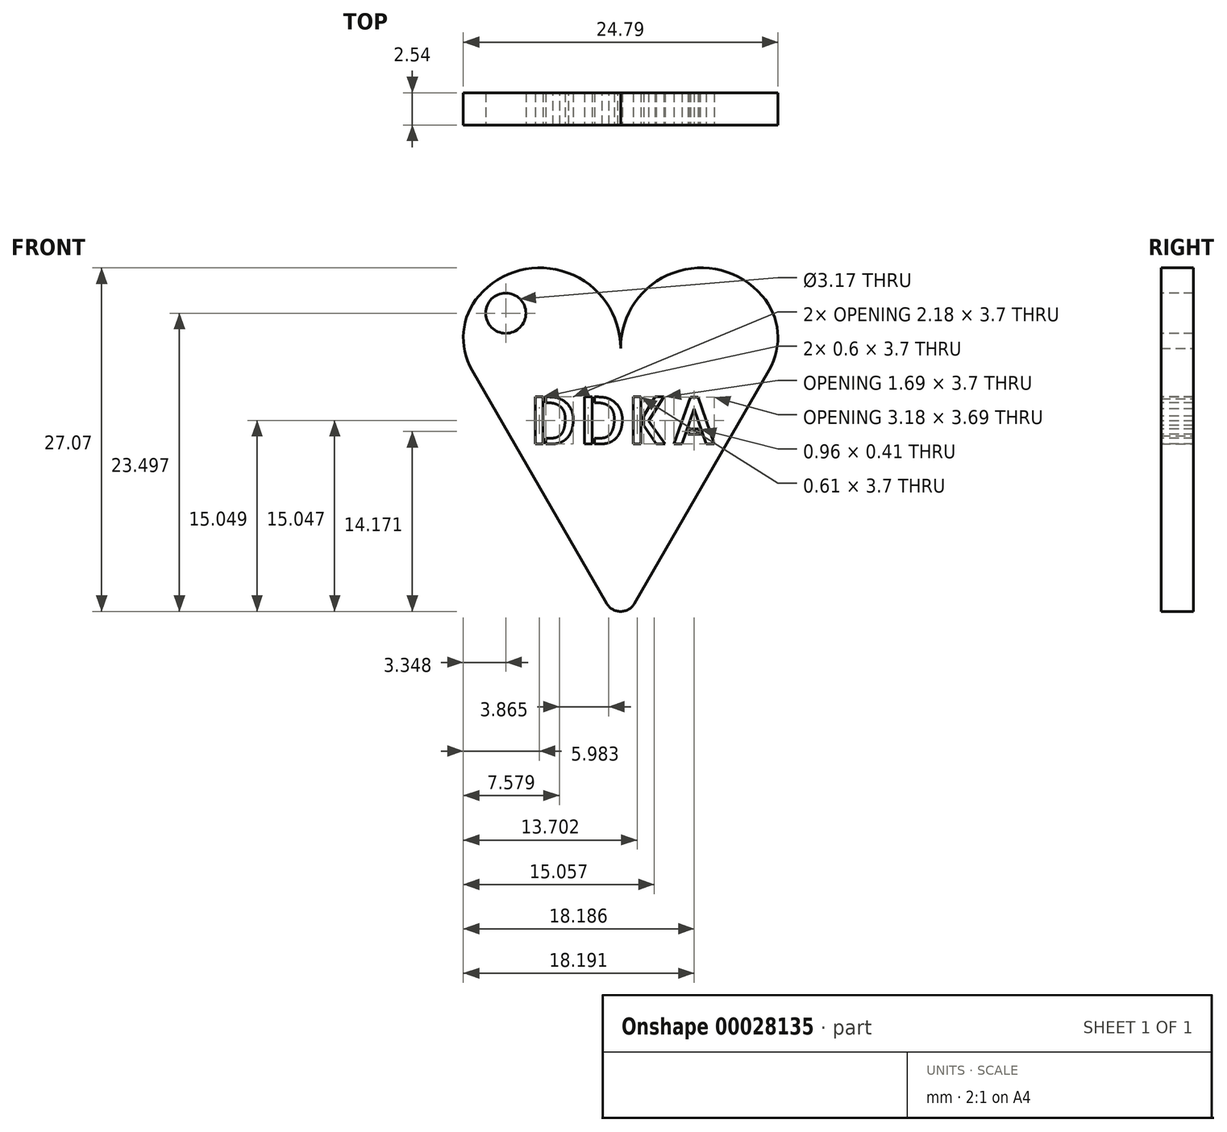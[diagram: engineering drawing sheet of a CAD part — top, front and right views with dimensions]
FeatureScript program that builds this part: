
annotation { "Feature Type Name" : "Feature", "Feature Type Description" : "" }
export const myFeature = defineFeature(function(context is Context, id is Id, definition is map)
    precondition{}
    {
        {
            var Q0;
            Q0=qCreatedBy(makeId("Front.planeOp"),FACE);
            var sketch = newSketch(context, id + "F0", { "sketchPlane" : qUnion([Q0])});
            skLineSegment(sketch, "E0", {"start": v(-11.28, 6.27) * mm, "end": v(1.42, -15.72) * mm});
            skLineSegment(sketch, "E1", {"start": v(1.42, -15.72) * mm, "end": v(14.12, 6.27) * mm});
            skLineSegment(sketch, "E2", {"start": v(14.12, 6.27) * mm, "end": v(-11.28, 6.27) * mm});
            skLineSegment(sketch, "E3", {"start": v(1.42, -15.72) * mm, "end": v(1.42, 38.6) * mm});
            skArc(sketch, "E4", {"start": v(1.42, 6.27) * mm, "mid": v(-4.93, 12.62) * mm, "end": v(-11.28, 6.27) * mm});
            skArc(sketch, "E5", {"start": v(14.12, 6.27) * mm, "mid": v(7.77, 12.62) * mm, "end": v(1.42, 6.27) * mm});
            skSolve(sketch);
        }
        {
            var Q0;
            {var subQ4=sQuery(id+"F0.wireOp",EDGE,"E0");Q0=makeQuery(id+"F0.imprint","IMPRINT",FACE,{"disambiguationData":[TD([[makeQuery(id+"F0.imprint","IMPRINT",EDGE,{"derivedFrom":subQ4}),1.0]])]});}
            var Q1;
            {var subQ0=sQuery(id+"F0.wireOp",EDGE,"E4");Q1=makeQuery(id+"F0.imprint","IMPRINT",FACE,{"disambiguationData":[TD([[makeQuery(id+"F0.imprint","IMPRINT",EDGE,{"derivedFrom":subQ0}),1.0]])]});}
            var Q2;
            {var subQ0=sQuery(id+"F0.wireOp",EDGE,"E5");Q2=makeQuery(id+"F0.imprint","IMPRINT",FACE,{"disambiguationData":[TD([[makeQuery(id+"F0.imprint","IMPRINT",EDGE,{"derivedFrom":subQ0}),1.0]])]});}
            var Q3;
            {var subQ4=sQuery(id+"F0.wireOp",EDGE,"E1");Q3=makeQuery(id+"F0.imprint","IMPRINT",FACE,{"disambiguationData":[TD([[makeQuery(id+"F0.imprint","IMPRINT",EDGE,{"derivedFrom":subQ4}),1.0]])]});}
            extrude(context, id + "F1", {"entities" : qUnion([Q0, Q1, Q2, Q3]), "depth" : 2.54 * mm});
        }
        {
            var Q0;
            Q0=makeQuery(id+"F1.opExtrude","SWEPT_EDGE",EDGE,{"disambiguationData":[OSD([sQuery(id+"F0.wireOp",EDGE,"E1"),sQuery(id+"F0.wireOp",EDGE,"E2"),sQuery(id+"F0.wireOp",EDGE,"E5")])]});
            fillet(context, id + "F2", {"entities" : qUnion([Q0]), "radius" : 5.08 * mm, "tangentPropagation" : true, "allowEdgeOverflow" : false});
        }
        {
            var Q0;
            Q0=makeQuery(id+"F1.opExtrude","SWEPT_EDGE",EDGE,{"disambiguationData":[OSD([sQuery(id+"F0.wireOp",EDGE,"E0"),sQuery(id+"F0.wireOp",EDGE,"E2"),sQuery(id+"F0.wireOp",EDGE,"E4")])]});
            fillet(context, id + "F3", {"entities" : qUnion([Q0]), "radius" : 5.08 * mm, "tangentPropagation" : true, "allowEdgeOverflow" : false});
        }
        {
            var Q0;
            Q0=makeQuery(id+"F1.opExtrude","CAP_FACE",FACE,{"disambiguationData":[OSD([sQuery(id+"F0.wireOp",EDGE,"E0"),sQuery(id+"F0.wireOp",EDGE,"E1"),sQuery(id+"F0.wireOp",EDGE,"E4"),sQuery(id+"F0.wireOp",EDGE,"E5")])],"isStart":false});
            var sketch = newSketch(context, id + "F4", { "sketchPlane" : qUnion([Q0])});
            skLineSegment(sketch, "E6", {"start": v(1.42, -13.18) * mm, "end": v(-9.38, 5.51) * mm});
            skLineSegment(sketch, "E7", {"start": v(1.42, -13.18) * mm, "end": v(12.21, 5.51) * mm});
            skPoint(sketch, "E8", {"position": v(1.42, 5) * mm});
            skLineSegment(sketch, "E9", {"start": v(1.42, 5) * mm, "end": v(-9.38, 5.51) * mm});
            skLineSegment(sketch, "E10", {"start": v(12.21, 5.51) * mm, "end": v(1.42, 5) * mm});
            skCircle(sketch, "E11", {"center": v(-7.63, 9.05) * mm, "radius": 1.59 * mm});
            skCircle(sketch, "E12", {"center": v(10.46, 9.05) * mm, "radius": 1.59 * mm});
            skLineSegment(sketch, "E13", {"start": v(-7.63, 9.05) * mm, "end": v(-9.38, 5.51) * mm});
            skLineSegment(sketch, "E14", {"start": v(10.46, 9.05) * mm, "end": v(12.21, 5.51) * mm});
            skSolve(sketch);
        }
        {
            var Q0;
            Q0=makeQuery(id+"F4.imprint","IMPRINT",FACE,{"disambiguationData":[TD([[makeQuery(id+"F4.imprint","IMPRINT",EDGE,{"derivedFrom":sQuery(id+"F4.wireOp",EDGE,"E11")}),1.0]])]});
            extrude(context, id + "F5", {"entities" : qUnion([Q0]), "operationType" : NewBodyOperationType.REMOVE, "oppositeDirection" : true, "depth" : 25.4 * mm});
        }
        {
            var Q0;
            Q0=makeQuery(id+"F1.opExtrude","CAP_FACE",FACE,{"disambiguationData":[OSD([sQuery(id+"F0.wireOp",EDGE,"E0"),sQuery(id+"F0.wireOp",EDGE,"E1"),sQuery(id+"F0.wireOp",EDGE,"E4"),sQuery(id+"F0.wireOp",EDGE,"E5")])],"isStart":false});
            var sketch = newSketch(context, id + "F6", { "sketchPlane" : qUnion([Q0])});
            skSolve(sketch);
        }
        {
            var Q0;
            Q0=makeQuery(id+"F1.opExtrude","SWEPT_EDGE",EDGE,{"disambiguationData":[OSD([sQuery(id+"F0.wireOp",EDGE,"E0"),sQuery(id+"F0.wireOp",EDGE,"E1"),sQuery(id+"F0.wireOp",EDGE,"E3")])]});
            fillet(context, id + "F7", {"entities" : qUnion([Q0]), "radius" : 1.27 * mm, "tangentPropagation" : true, "allowEdgeOverflow" : false});
        }
        {
            var Q0;
            {var subQ4=sQuery(id+"F0.wireOp",EDGE,"E5");Q0=makeQuery(id+"F6.imprint","IMPRINT",FACE,{"disambiguationData":[TD([[makeQuery(id+"F6.imprint","IMPRINT",EDGE,{"derivedFrom":makeQuery(id+"F1.opExtrude","CAP_EDGE",EDGE,{"disambiguationData":[OSD([subQ4])],"isStart":false})}),1.0]])]});}
            var sketch = newSketch(context, id + "F8", { "sketchPlane" : qUnion([Q0])});
            skText(sketch, "E15", { "text": "DDKA", "fontName": "AllertaStencil-Regular.ttf"});
            const initialGuessF8  = {"E15": [-0.00578, -0.00125, 1, 0, 0.0037]};
            skSetInitialGuess(sketch, initialGuessF8);
            skSolve(sketch);
        }
        {
            var Q0;
            Q0 = qSketchRegion(id + "F8", true);
            extrude(context, id + "F9", {"entities" : qUnion([Q0]), "operationType" : NewBodyOperationType.REMOVE, "oppositeDirection" : true, "depth" : 25.4 * mm});
        }
    });
